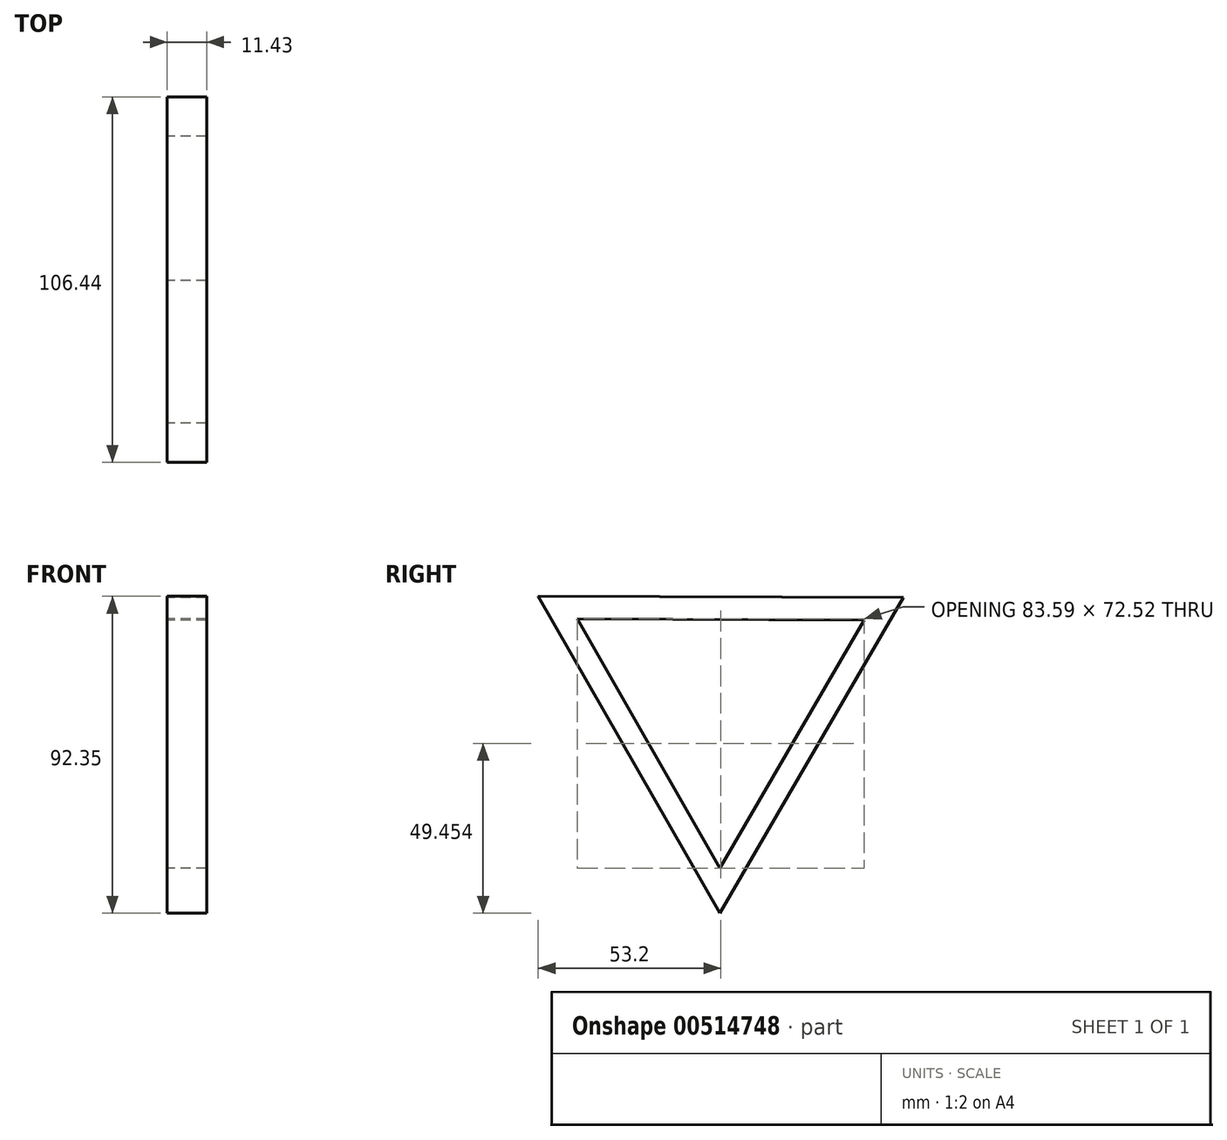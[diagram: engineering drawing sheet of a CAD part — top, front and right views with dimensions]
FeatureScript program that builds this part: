
annotation { "Feature Type Name" : "Feature", "Feature Type Description" : "" }
export const myFeature = defineFeature(function(context is Context, id is Id, definition is map)
    precondition{}
    {
        {
            var Q0;
            Q0=qCreatedBy(makeId("Right.planeOp"),FACE);
            var sketch = newSketch(context, id + "F0", { "sketchPlane" : qUnion([Q0])});
            skCircle(sketch, "E0.cCircle", {"center": v(0, 0) * mm, "radius": 24.13 * mm, "construction": true});
            skLineSegment(sketch, "E0.0", {"start": v(-0.16, -48.26) * mm, "end": v(-41.71, 24.27) * mm});
            skLineSegment(sketch, "E0.1", {"start": v(-41.71, 24.27) * mm, "end": v(41.87, 24) * mm});
            skLineSegment(sketch, "E0.2", {"start": v(41.87, 24) * mm, "end": v(-0.16, -48.26) * mm});
            skPoint(sketch, "E0.0.midPoint", {"position": v(-20.94, -12) * mm});
            skCircle(sketch, "E1.cCircle", {"center": v(0, 0) * mm, "radius": 30.73 * mm, "construction": true});
            skLineSegment(sketch, "E1.0", {"start": v(53.32, 30.55) * mm, "end": v(-0.2, -61.45) * mm});
            skLineSegment(sketch, "E1.1", {"start": v(-0.2, -61.45) * mm, "end": v(-53.12, 30.9) * mm});
            skLineSegment(sketch, "E1.2", {"start": v(-53.12, 30.9) * mm, "end": v(53.32, 30.55) * mm});
            skPoint(sketch, "E1.0.midPoint", {"position": v(26.56, -15.45) * mm});
            skSolve(sketch);
        }
        {
            var Q0;
            Q0 = qSketchRegion(id + "F0", true);
            extrude(context, id + "F1", {"entities" : qUnion([Q0]), "depth" : 11.43 * mm, "offsetDistance" : 25.4 * mm});
        }
    });
